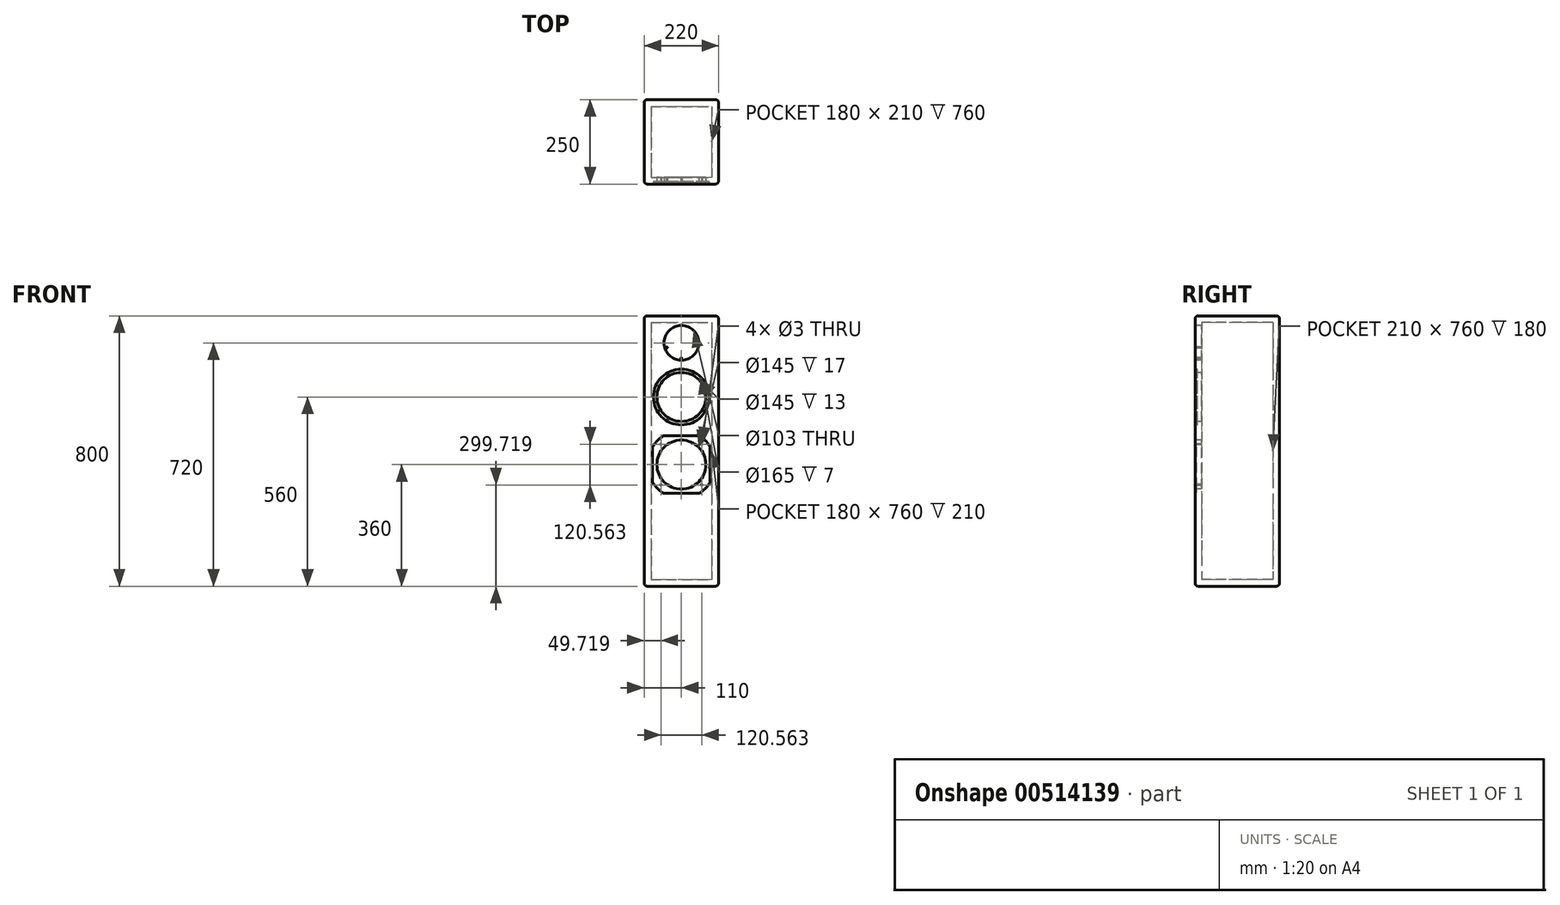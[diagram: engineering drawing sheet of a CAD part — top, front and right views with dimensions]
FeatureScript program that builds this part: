
annotation { "Feature Type Name" : "Feature", "Feature Type Description" : "" }
export const myFeature = defineFeature(function(context is Context, id is Id, definition is map)
    precondition{}
    {
        {
            var Q0;
            Q0=qCreatedBy(makeId("Top.planeOp"),FACE);
            var sketch = newSketch(context, id + "F0", { "sketchPlane" : qUnion([Q0])});
            skLineSegment(sketch, "E0.bottom", {"start": v(-110, 125) * mm, "end": v(110, 125) * mm});
            skLineSegment(sketch, "E0.top", {"start": v(-110, -125) * mm, "end": v(110, -125) * mm});
            skLineSegment(sketch, "E0.left", {"start": v(-110, 125) * mm, "end": v(-110, -125) * mm});
            skLineSegment(sketch, "E0.right", {"start": v(110, 125) * mm, "end": v(110, -125) * mm});
            skPoint(sketch, "E0.middle", {"position": v(0, 0) * mm});
            skLineSegment(sketch, "E1.bottom", {"start": v(-90, 105) * mm, "end": v(90, 105) * mm});
            skLineSegment(sketch, "E1.top", {"start": v(-90, -105) * mm, "end": v(90, -105) * mm});
            skLineSegment(sketch, "E1.left", {"start": v(-90, 105) * mm, "end": v(-90, -105) * mm});
            skLineSegment(sketch, "E1.right", {"start": v(90, 105) * mm, "end": v(90, -105) * mm});
            skSolve(sketch);
        }
        {
            var Q0;
            Q0=makeQuery(id+"F0.imprint","IMPRINT",FACE,{"disambiguationData":[TD([[makeQuery(id+"F0.imprint","IMPRINT",EDGE,{"derivedFrom":sQuery(id+"F0.wireOp",EDGE,"E1.bottom")}),-1.0]])]});
            extrude(context, id + "F1", {"entities" : qUnion([Q0]), "depth" : 20 * mm, "offsetDistance" : 25 * mm});
        }
        {
            var Q0;
            Q0=makeQuery(id+"F0.imprint","IMPRINT",FACE,{"disambiguationData":[TD([[makeQuery(id+"F0.imprint","IMPRINT",EDGE,{"derivedFrom":sQuery(id+"F0.wireOp",EDGE,"E0.bottom")}),-1.0]])]});
            extrude(context, id + "F2", {"entities" : qUnion([Q0]), "operationType" : NewBodyOperationType.ADD, "depth" : 800 * mm, "offsetDistance" : 25 * mm});
        }
        {
            var Q0;
            Q0=makeQuery(id+"F2.opExtrude","CAP_FACE",FACE,{"disambiguationData":[OSD([sQuery(id+"F0.wireOp",EDGE,"E0.bottom"),sQuery(id+"F0.wireOp",EDGE,"E0.top"),sQuery(id+"F0.wireOp",EDGE,"E0.left"),sQuery(id+"F0.wireOp",EDGE,"E0.right"),sQuery(id+"F0.wireOp",EDGE,"E1.bottom"),sQuery(id+"F0.wireOp",EDGE,"E1.top"),sQuery(id+"F0.wireOp",EDGE,"E1.left"),sQuery(id+"F0.wireOp",EDGE,"E1.right")])],"isStart":false});
            var sketch = newSketch(context, id + "F3", { "sketchPlane" : qUnion([Q0])});
            skLineSegment(sketch, "E2.0.0", {"start": v(-90, 105) * mm, "end": v(-90, -105) * mm});
            skLineSegment(sketch, "E2.0.1", {"start": v(-90, -105) * mm, "end": v(90, -105) * mm});
            skLineSegment(sketch, "E2.0.2", {"start": v(90, -105) * mm, "end": v(90, 105) * mm});
            skLineSegment(sketch, "E2.0.3", {"start": v(90, 105) * mm, "end": v(-90, 105) * mm});
            skSolve(sketch);
        }
        {
            var Q0;
            Q0=makeQuery(id+"F3.imprint","IMPRINT",FACE,{"disambiguationData":[TD([[makeQuery(id+"F3.imprint","IMPRINT",EDGE,{"derivedFrom":sQuery(id+"F3.wireOp",EDGE,"E2.0.0")}),1.0]])]});
            extrude(context, id + "F4", {"entities" : qUnion([Q0]), "operationType" : NewBodyOperationType.ADD, "depth" : -20 * mm, "offsetDistance" : 25 * mm});
        }
        {
            var Q0;
            Q0=makeQuery(id+"F2.opExtrude","SWEPT_FACE",FACE,{"disambiguationData":[OSD([sQuery(id+"F0.wireOp",EDGE,"E0.top")])]});
            var sketch = newSketch(context, id + "F5", { "sketchPlane" : qUnion([Q0])});
            skLineSegment(sketch, "E3", {"start": v(0, 800) * mm, "end": v(0, 0) * mm});
            skLineSegment(sketch, "E4.bottom", {"start": v(85, 445) * mm, "end": v(-85, 445) * mm});
            skLineSegment(sketch, "E4.top", {"start": v(85, 275) * mm, "end": v(-85, 275) * mm});
            skLineSegment(sketch, "E4.left", {"start": v(85, 445) * mm, "end": v(85, 275) * mm});
            skLineSegment(sketch, "E4.right", {"start": v(-85, 445) * mm, "end": v(-85, 275) * mm});
            skPoint(sketch, "E4.middle", {"position": v(0, 360) * mm});
            skCircle(sketch, "E5", {"center": v(0, 360) * mm, "radius": 100 * mm});
            skCircle(sketch, "E6", {"center": v(0, 720) * mm, "radius": 51.5 * mm});
            skCircle(sketch, "E7", {"center": v(0, 720) * mm, "radius": 45 * mm});
            skCircle(sketch, "E8", {"center": v(0, 720) * mm, "radius": 40 * mm});
            skCircle(sketch, "E9", {"center": v(0, 360) * mm, "radius": 72.5 * mm});
            skCircle(sketch, "E10", {"center": v(0, 560) * mm, "radius": 72.5 * mm});
            skCircle(sketch, "E11", {"center": v(0, 560) * mm, "radius": 82.5 * mm});
            skCircle(sketch, "E12", {"center": v(0, 675) * mm, "radius": 1.5 * mm});
            skCircle(sketch, "E13.1.0", {"center": v(42.8, 706.1) * mm, "radius": 1.5 * mm});
            skCircle(sketch, "E13.2.0", {"center": v(26.45, 756.4) * mm, "radius": 1.5 * mm});
            skCircle(sketch, "E13.3.0", {"center": v(-26.45, 756.4) * mm, "radius": 1.5 * mm});
            skCircle(sketch, "E13.4.0", {"center": v(-42.8, 706.1) * mm, "radius": 1.5 * mm});
            skCircle(sketch, "E14", {"center": v(-60.28, 420.28) * mm, "radius": 1.5 * mm});
            skLineSegment(sketch, "E15", {"start": v(-85, 445) * mm, "end": v(0, 360) * mm, "construction": true});
            skCircle(sketch, "E16.1.0", {"center": v(-60.28, 299.72) * mm, "radius": 1.5 * mm});
            skCircle(sketch, "E16.2.0", {"center": v(60.28, 299.72) * mm, "radius": 1.5 * mm});
            skCircle(sketch, "E16.3.0", {"center": v(60.28, 420.28) * mm, "radius": 1.5 * mm});
            skSolve(sketch);
        }
        {
            var Q0;
            Q0=makeQuery(id+"F5.imprint","IMPRINT",FACE,{"disambiguationData":[TD([[makeQuery(id+"F5.imprint","IMPRINT",EDGE,{"derivedFrom":sQuery(id+"F5.wireOp",EDGE,"E10")}),1.0]])]});
            var Q1;
            Q1=makeQuery(id+"F5.imprint","IMPRINT",FACE,{"disambiguationData":[TD([[makeQuery(id+"F5.imprint","IMPRINT",EDGE,{"derivedFrom":sQuery(id+"F5.wireOp",EDGE,"E9")}),1.0]])]});
            var Q2;
            Q2=makeQuery(id+"F5.imprint","IMPRINT",FACE,{"disambiguationData":[TD([[makeQuery(id+"F5.imprint","IMPRINT",EDGE,{"derivedFrom":sQuery(id+"F5.wireOp",EDGE,"E8")}),1.0]])]});
            var Q3;
            {var subQ0=sQuery(id+"F5.wireOp",EDGE,"E12");var subQ1=sQuery(id+"F5.wireOp",EDGE,"E7");var subQ2=makeQuery(id+"F5.imprint","INTERSECT",VERTEX,{"disambiguationData":[OD(0.0)],"derivedFrom":[subQ1,subQ0]});Q3=makeQuery(id+"F5.imprint","IMPRINT",FACE,{"disambiguationData":[TD([[makeQuery(id+"F5.imprint","IMPRINT",EDGE,{"disambiguationData":[TD([[subQ2,-1.0]])],"derivedFrom":subQ1}),1.0]])]});}
            var Q4;
            {var subQ0=sQuery(id+"F5.wireOp",EDGE,"E12");var subQ1=sQuery(id+"F5.wireOp",EDGE,"E7");var subQ2=makeQuery(id+"F5.imprint","INTERSECT",VERTEX,{"disambiguationData":[OD(0.0)],"derivedFrom":[subQ1,subQ0]});Q4=makeQuery(id+"F5.imprint","IMPRINT",FACE,{"disambiguationData":[TD([[makeQuery(id+"F5.imprint","IMPRINT",EDGE,{"disambiguationData":[TD([[subQ2,-1.0]])],"derivedFrom":subQ1}),-1.0]])]});}
            var Q5;
            {var subQ0=sQuery(id+"F5.wireOp",EDGE,"E13.4.0");var subQ1=sQuery(id+"F5.wireOp",EDGE,"E7");var subQ2=makeQuery(id+"F5.imprint","INTERSECT",VERTEX,{"disambiguationData":[OD(0.0)],"derivedFrom":[subQ1,subQ0]});Q5=makeQuery(id+"F5.imprint","IMPRINT",FACE,{"disambiguationData":[TD([[makeQuery(id+"F5.imprint","IMPRINT",EDGE,{"disambiguationData":[TD([[subQ2,1.0]])],"derivedFrom":subQ1}),1.0]])]});}
            var Q6;
            {var subQ0=sQuery(id+"F5.wireOp",EDGE,"E13.4.0");var subQ1=sQuery(id+"F5.wireOp",EDGE,"E7");var subQ2=makeQuery(id+"F5.imprint","INTERSECT",VERTEX,{"disambiguationData":[OD(0.0)],"derivedFrom":[subQ1,subQ0]});Q6=makeQuery(id+"F5.imprint","IMPRINT",FACE,{"disambiguationData":[TD([[makeQuery(id+"F5.imprint","IMPRINT",EDGE,{"disambiguationData":[TD([[subQ2,1.0]])],"derivedFrom":subQ1}),-1.0]])]});}
            var Q7;
            {var subQ0=sQuery(id+"F5.wireOp",EDGE,"E13.3.0");var subQ1=sQuery(id+"F5.wireOp",EDGE,"E7");var subQ2=makeQuery(id+"F5.imprint","INTERSECT",VERTEX,{"disambiguationData":[OD(0.0)],"derivedFrom":[subQ1,subQ0]});Q7=makeQuery(id+"F5.imprint","IMPRINT",FACE,{"disambiguationData":[TD([[makeQuery(id+"F5.imprint","IMPRINT",EDGE,{"disambiguationData":[TD([[subQ2,-1.0]])],"derivedFrom":subQ1}),1.0]])]});}
            var Q8;
            {var subQ0=sQuery(id+"F5.wireOp",EDGE,"E13.3.0");var subQ1=sQuery(id+"F5.wireOp",EDGE,"E7");var subQ2=makeQuery(id+"F5.imprint","INTERSECT",VERTEX,{"disambiguationData":[OD(0.0)],"derivedFrom":[subQ1,subQ0]});Q8=makeQuery(id+"F5.imprint","IMPRINT",FACE,{"disambiguationData":[TD([[makeQuery(id+"F5.imprint","IMPRINT",EDGE,{"disambiguationData":[TD([[subQ2,-1.0]])],"derivedFrom":subQ1}),-1.0]])]});}
            var Q9;
            {var subQ0=sQuery(id+"F5.wireOp",EDGE,"E13.2.0");var subQ1=sQuery(id+"F5.wireOp",EDGE,"E7");var subQ2=makeQuery(id+"F5.imprint","INTERSECT",VERTEX,{"disambiguationData":[OD(0.0)],"derivedFrom":[subQ1,subQ0]});Q9=makeQuery(id+"F5.imprint","IMPRINT",FACE,{"disambiguationData":[TD([[makeQuery(id+"F5.imprint","IMPRINT",EDGE,{"disambiguationData":[TD([[subQ2,-1.0]])],"derivedFrom":subQ1}),1.0]])]});}
            var Q10;
            {var subQ0=sQuery(id+"F5.wireOp",EDGE,"E13.2.0");var subQ1=sQuery(id+"F5.wireOp",EDGE,"E7");var subQ2=makeQuery(id+"F5.imprint","INTERSECT",VERTEX,{"disambiguationData":[OD(0.0)],"derivedFrom":[subQ1,subQ0]});Q10=makeQuery(id+"F5.imprint","IMPRINT",FACE,{"disambiguationData":[TD([[makeQuery(id+"F5.imprint","IMPRINT",EDGE,{"disambiguationData":[TD([[subQ2,-1.0]])],"derivedFrom":subQ1}),-1.0]])]});}
            var Q11;
            {var subQ0=sQuery(id+"F5.wireOp",EDGE,"E13.1.0");var subQ1=sQuery(id+"F5.wireOp",EDGE,"E7");var subQ2=makeQuery(id+"F5.imprint","INTERSECT",VERTEX,{"disambiguationData":[OD(0.0)],"derivedFrom":[subQ1,subQ0]});Q11=makeQuery(id+"F5.imprint","IMPRINT",FACE,{"disambiguationData":[TD([[makeQuery(id+"F5.imprint","IMPRINT",EDGE,{"disambiguationData":[TD([[subQ2,-1.0]])],"derivedFrom":subQ1}),1.0]])]});}
            var Q12;
            {var subQ0=sQuery(id+"F5.wireOp",EDGE,"E13.1.0");var subQ1=sQuery(id+"F5.wireOp",EDGE,"E7");var subQ2=makeQuery(id+"F5.imprint","INTERSECT",VERTEX,{"disambiguationData":[OD(0.0)],"derivedFrom":[subQ1,subQ0]});Q12=makeQuery(id+"F5.imprint","IMPRINT",FACE,{"disambiguationData":[TD([[makeQuery(id+"F5.imprint","IMPRINT",EDGE,{"disambiguationData":[TD([[subQ2,-1.0]])],"derivedFrom":subQ1}),-1.0]])]});}
            var Q13;
            Q13=makeQuery(id+"F5.imprint","IMPRINT",FACE,{"disambiguationData":[TD([[makeQuery(id+"F5.imprint","IMPRINT",EDGE,{"derivedFrom":sQuery(id+"F5.wireOp",EDGE,"E14")}),1.0]])]});
            var Q14;
            Q14=makeQuery(id+"F5.imprint","IMPRINT",FACE,{"disambiguationData":[TD([[makeQuery(id+"F5.imprint","IMPRINT",EDGE,{"derivedFrom":sQuery(id+"F5.wireOp",EDGE,"E16.3.0")}),1.0]])]});
            var Q15;
            Q15=makeQuery(id+"F5.imprint","IMPRINT",FACE,{"disambiguationData":[TD([[makeQuery(id+"F5.imprint","IMPRINT",EDGE,{"derivedFrom":sQuery(id+"F5.wireOp",EDGE,"E16.2.0")}),1.0]])]});
            var Q16;
            Q16=makeQuery(id+"F5.imprint","IMPRINT",FACE,{"disambiguationData":[TD([[makeQuery(id+"F5.imprint","IMPRINT",EDGE,{"derivedFrom":sQuery(id+"F5.wireOp",EDGE,"E16.1.0")}),1.0]])]});
            extrude(context, id + "F6", {"entities" : qUnion([Q0, Q1, Q2, Q3, Q4, Q5, Q6, Q7, Q8, Q9, Q10, Q11, Q12, Q13, Q14, Q15, Q16]), "operationType" : NewBodyOperationType.REMOVE, "oppositeDirection" : true, "depth" : 20 * mm, "offsetDistance" : 25 * mm});
        }
        {
            var Q0;
            Q0=makeQuery(id+"F5.imprint","IMPRINT",FACE,{"disambiguationData":[TD([[makeQuery(id+"F5.imprint","IMPRINT",EDGE,{"derivedFrom":sQuery(id+"F5.wireOp",EDGE,"E10")}),-1.0]])]});
            extrude(context, id + "F7", {"entities" : qUnion([Q0]), "operationType" : NewBodyOperationType.REMOVE, "oppositeDirection" : true, "depth" : 7 * mm, "offsetDistance" : 25 * mm});
        }
        {
            var Q0;
            Q0=makeQuery(id+"F5.imprint","IMPRINT",FACE,{"disambiguationData":[TD([[makeQuery(id+"F5.imprint","IMPRINT",EDGE,{"derivedFrom":sQuery(id+"F5.wireOp",EDGE,"E9")}),-1.0]])]});
            var Q1;
            Q1=makeQuery(id+"F5.imprint","IMPRINT",FACE,{"disambiguationData":[TD([[makeQuery(id+"F5.imprint","IMPRINT",EDGE,{"derivedFrom":sQuery(id+"F5.wireOp",EDGE,"E6")}),1.0]])]});
            var Q2;
            Q2=makeQuery(id+"F5.imprint","IMPRINT",FACE,{"disambiguationData":[TD([[makeQuery(id+"F5.imprint","IMPRINT",EDGE,{"derivedFrom":sQuery(id+"F5.wireOp",EDGE,"E8")}),-1.0]])]});
            extrude(context, id + "F8", {"entities" : qUnion([Q0, Q1, Q2]), "operationType" : NewBodyOperationType.REMOVE, "oppositeDirection" : true, "depth" : 3 * mm, "offsetDistance" : 25 * mm});
        }
        {
            var Q0;
            Q0=makeQuery(id+"F2.opExtrude","CAP_EDGE",EDGE,{"disambiguationData":[OSD([sQuery(id+"F0.wireOp",EDGE,"E0.top")])],"isStart":false});
            var Q1;
            Q1=makeQuery(id+"F2.opExtrude","CAP_EDGE",EDGE,{"disambiguationData":[OSD([sQuery(id+"F0.wireOp",EDGE,"E0.right")])],"isStart":false});
            var Q2;
            Q2=makeQuery(id+"F2.opExtrude","SWEPT_EDGE",EDGE,{"disambiguationData":[OSD([sQuery(id+"F0.wireOp",EDGE,"E0.top"),sQuery(id+"F0.wireOp",EDGE,"E0.right")])]});
            var Q3;
            Q3=makeQuery(id+"F2.opExtrude","SWEPT_EDGE",EDGE,{"disambiguationData":[OSD([sQuery(id+"F0.wireOp",EDGE,"E0.bottom"),sQuery(id+"F0.wireOp",EDGE,"E0.right")])]});
            var Q4;
            Q4=makeQuery(id+"F2.opExtrude","CAP_EDGE",EDGE,{"disambiguationData":[OSD([sQuery(id+"F0.wireOp",EDGE,"E0.bottom")])],"isStart":false});
            var Q5;
            Q5=makeQuery(id+"F2.opExtrude","CAP_EDGE",EDGE,{"disambiguationData":[OSD([sQuery(id+"F0.wireOp",EDGE,"E0.left")])],"isStart":false});
            var Q6;
            Q6=makeQuery(id+"F2.opExtrude","SWEPT_EDGE",EDGE,{"disambiguationData":[OSD([sQuery(id+"F0.wireOp",EDGE,"E0.top"),sQuery(id+"F0.wireOp",EDGE,"E0.left")])]});
            var Q7;
            Q7=makeQuery(id+"F2.opExtrude","CAP_EDGE",EDGE,{"disambiguationData":[OSD([sQuery(id+"F0.wireOp",EDGE,"E0.top")])],"isStart":true});
            var Q8;
            Q8=makeQuery(id+"F2.opExtrude","SWEPT_EDGE",EDGE,{"disambiguationData":[OSD([sQuery(id+"F0.wireOp",EDGE,"E0.bottom"),sQuery(id+"F0.wireOp",EDGE,"E0.left")])]});
            var Q9;
            Q9=makeQuery(id+"F2.opExtrude","CAP_EDGE",EDGE,{"disambiguationData":[OSD([sQuery(id+"F0.wireOp",EDGE,"E0.left")])],"isStart":true});
            var Q10;
            Q10=makeQuery(id+"F2.opExtrude","CAP_EDGE",EDGE,{"disambiguationData":[OSD([sQuery(id+"F0.wireOp",EDGE,"E0.right")])],"isStart":true});
            var Q11;
            Q11=makeQuery(id+"F2.opExtrude","CAP_EDGE",EDGE,{"disambiguationData":[OSD([sQuery(id+"F0.wireOp",EDGE,"E0.bottom")])],"isStart":true});
            fillet(context, id + "F9", {"entities" : qUnion([Q0, Q1, Q2, Q3, Q4, Q5, Q6, Q7, Q8, Q9, Q10, Q11]), "radius" : 9.5 * mm, "tangentPropagation" : true, "allowEdgeOverflow" : false});
        }
    });
